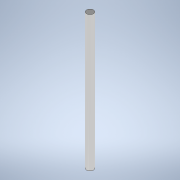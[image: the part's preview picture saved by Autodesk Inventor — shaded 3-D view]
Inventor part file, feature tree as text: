
AUTODESK INVENTOR PART (.ipt)
format: ipt  version: 2022 (Build 260153000, 153)  size: 93,184 bytes
history: native  units: mm
features: extrude x1, sketch x1
ambient origin geometry x8: Origin, YZ Plane, XZ Plane, XY Plane, X Axis, Y Axis, Z Axis, Center Point
bodies: Solid1 (feature_tree)
feature tree (2):
  extrude  "Extrusion1"  Depth=39.5mm TaperAngle=0.0deg
  sketch  "Sketch1"  dims[d0=2.0mm d1=39.5mm d2=0.0mm]
